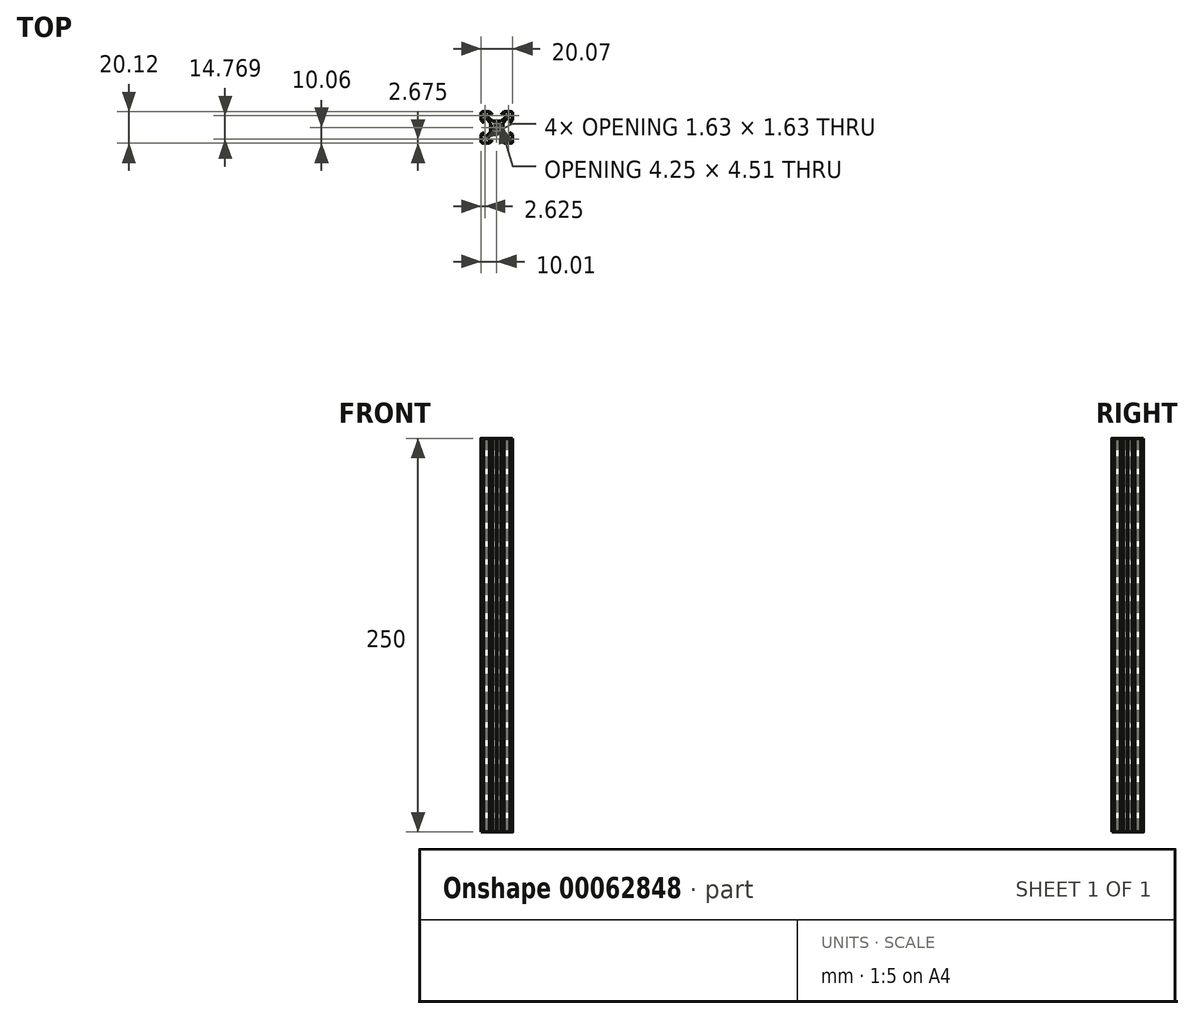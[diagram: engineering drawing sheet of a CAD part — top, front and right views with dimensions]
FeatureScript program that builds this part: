
annotation { "Feature Type Name" : "Feature", "Feature Type Description" : "" }
export const myFeature = defineFeature(function(context is Context, id is Id, definition is map)
    precondition{}
    {
        {
            var Q0;
            Q0=qCreatedBy(makeId("Top.planeOp"),FACE);
            var sketch = newSketch(context, id + "F0", { "sketchPlane" : qUnion([Q0])});
            skFitSpline(sketch, "E0", {"points": [v(-8.5, 10) * mm, v(-8.9, 10) * mm, v(-9.28, 9.84) * mm, v(-9.56, 9.56) * mm]});
            skFitSpline(sketch, "E1", {"points": [v(-9.56, 9.56) * mm, v(-9.84, 9.28) * mm, v(-10, 8.9) * mm, v(-10, 8.5) * mm]});
            skLineSegment(sketch, "E2", {"start": v(-10, 8.5) * mm, "end": v(-10, 4.64) * mm});
            skLineSegment(sketch, "E3", {"start": v(-10, 4.64) * mm, "end": v(-8.2, 2.84) * mm});
            skLineSegment(sketch, "E4", {"start": v(-8.2, 5.5) * mm, "end": v(-8.2, 2.84) * mm});
            skLineSegment(sketch, "E5", {"start": v(-8.2, 5.5) * mm, "end": v(-6.56, 5.5) * mm});
            skLineSegment(sketch, "E6", {"start": v(-6.56, 5.5) * mm, "end": v(-3.9, 2.84) * mm});
            skLineSegment(sketch, "E7", {"start": v(-3.9, 2.84) * mm, "end": v(-3.9, 0.2) * mm});
            skLineSegment(sketch, "E8", {"start": v(-3.9, 0.2) * mm, "end": v(-3.7, 0) * mm});
            skLineSegment(sketch, "E9", {"start": v(-3.9, -0.2) * mm, "end": v(-3.7, 0) * mm});
            skLineSegment(sketch, "E10", {"start": v(-3.9, -2.84) * mm, "end": v(-3.9, -0.2) * mm});
            skLineSegment(sketch, "E11", {"start": v(-6.56, -5.5) * mm, "end": v(-3.9, -2.84) * mm});
            skLineSegment(sketch, "E12", {"start": v(-8.2, -5.5) * mm, "end": v(-6.56, -5.5) * mm});
            skLineSegment(sketch, "E13", {"start": v(-8.2, -5.5) * mm, "end": v(-8.2, -2.84) * mm});
            skLineSegment(sketch, "E14", {"start": v(-10, -4.64) * mm, "end": v(-8.2, -2.84) * mm});
            skFitSpline(sketch, "E15", {"points": [v(-10, -8.5) * mm, v(-10, -8.9) * mm, v(-9.84, -9.28) * mm, v(-9.56, -9.56) * mm]});
            skFitSpline(sketch, "E16", {"points": [v(-9.56, -9.56) * mm, v(-9.28, -9.84) * mm, v(-8.9, -10) * mm, v(-8.5, -10) * mm]});
            skLineSegment(sketch, "E17", {"start": v(-10, -8.5) * mm, "end": v(-10, -4.64) * mm});
            skLineSegment(sketch, "E18", {"start": v(-8.5, -10) * mm, "end": v(-4.64, -10) * mm});
            skLineSegment(sketch, "E19", {"start": v(-4.64, -10) * mm, "end": v(-2.84, -8.2) * mm});
            skLineSegment(sketch, "E20", {"start": v(-2.84, -8.2) * mm, "end": v(-5.5, -8.2) * mm});
            skLineSegment(sketch, "E21", {"start": v(-5.5, -8.2) * mm, "end": v(-5.5, -6.56) * mm});
            skLineSegment(sketch, "E22", {"start": v(-5.5, -6.56) * mm, "end": v(-2.84, -3.9) * mm});
            skLineSegment(sketch, "E23", {"start": v(-0.2, -3.9) * mm, "end": v(-2.84, -3.9) * mm});
            skLineSegment(sketch, "E24", {"start": v(-0.2, -3.9) * mm, "end": v(0, -3.7) * mm});
            skLineSegment(sketch, "E25", {"start": v(0.2, -3.9) * mm, "end": v(0, -3.7) * mm});
            skLineSegment(sketch, "E26", {"start": v(0.2, -3.9) * mm, "end": v(2.84, -3.9) * mm});
            skLineSegment(sketch, "E27", {"start": v(5.5, -6.56) * mm, "end": v(2.84, -3.9) * mm});
            skLineSegment(sketch, "E28", {"start": v(5.5, -8.2) * mm, "end": v(5.5, -6.56) * mm});
            skLineSegment(sketch, "E29", {"start": v(2.84, -8.2) * mm, "end": v(5.5, -8.2) * mm});
            skLineSegment(sketch, "E30", {"start": v(4.64, -10) * mm, "end": v(2.84, -8.2) * mm});
            skFitSpline(sketch, "E31", {"points": [v(8.5, -10) * mm, v(9.33, -10) * mm, v(10, -9.33) * mm, v(10, -8.5) * mm]});
            skLineSegment(sketch, "E32", {"start": v(8.5, -10) * mm, "end": v(4.64, -10) * mm});
            skLineSegment(sketch, "E33", {"start": v(10, -8.5) * mm, "end": v(10, -4.64) * mm});
            skLineSegment(sketch, "E34", {"start": v(10, -4.64) * mm, "end": v(8.2, -2.84) * mm});
            skLineSegment(sketch, "E35", {"start": v(8.2, -5.5) * mm, "end": v(8.2, -2.84) * mm});
            skLineSegment(sketch, "E36", {"start": v(8.2, -5.5) * mm, "end": v(6.56, -5.5) * mm});
            skLineSegment(sketch, "E37", {"start": v(6.56, -5.5) * mm, "end": v(3.9, -2.84) * mm});
            skLineSegment(sketch, "E38", {"start": v(3.9, -2.84) * mm, "end": v(3.9, -0.2) * mm});
            skLineSegment(sketch, "E39", {"start": v(3.9, -0.2) * mm, "end": v(3.7, 0) * mm});
            skLineSegment(sketch, "E40", {"start": v(3.9, 0.2) * mm, "end": v(3.7, 0) * mm});
            skLineSegment(sketch, "E41", {"start": v(3.9, 2.84) * mm, "end": v(3.9, 0.2) * mm});
            skLineSegment(sketch, "E42", {"start": v(6.56, 5.5) * mm, "end": v(3.9, 2.84) * mm});
            skLineSegment(sketch, "E43", {"start": v(8.2, 5.5) * mm, "end": v(6.56, 5.5) * mm});
            skLineSegment(sketch, "E44", {"start": v(8.2, 5.5) * mm, "end": v(8.2, 2.84) * mm});
            skLineSegment(sketch, "E45", {"start": v(10, 4.64) * mm, "end": v(8.2, 2.84) * mm});
            skFitSpline(sketch, "E46", {"points": [v(10, 8.5) * mm, v(10, 9.33) * mm, v(9.33, 10) * mm, v(8.5, 10) * mm]});
            skLineSegment(sketch, "E47", {"start": v(10, 8.5) * mm, "end": v(10, 4.64) * mm});
            skLineSegment(sketch, "E48", {"start": v(8.5, 10) * mm, "end": v(4.64, 10) * mm});
            skLineSegment(sketch, "E49", {"start": v(4.64, 10) * mm, "end": v(2.84, 8.2) * mm});
            skLineSegment(sketch, "E50", {"start": v(2.84, 8.2) * mm, "end": v(5.5, 8.2) * mm});
            skLineSegment(sketch, "E51", {"start": v(5.5, 8.2) * mm, "end": v(5.5, 6.56) * mm});
            skLineSegment(sketch, "E52", {"start": v(5.5, 6.56) * mm, "end": v(2.84, 3.9) * mm});
            skLineSegment(sketch, "E53", {"start": v(0.2, 3.9) * mm, "end": v(2.84, 3.9) * mm});
            skLineSegment(sketch, "E54", {"start": v(0.2, 3.9) * mm, "end": v(0, 3.7) * mm});
            skLineSegment(sketch, "E55", {"start": v(-0.2, 3.9) * mm, "end": v(0, 3.7) * mm});
            skLineSegment(sketch, "E56", {"start": v(-0.2, 3.9) * mm, "end": v(-2.84, 3.9) * mm});
            skLineSegment(sketch, "E57", {"start": v(-5.5, 6.56) * mm, "end": v(-2.84, 3.9) * mm});
            skLineSegment(sketch, "E58", {"start": v(-5.5, 8.2) * mm, "end": v(-5.5, 6.56) * mm});
            skLineSegment(sketch, "E59", {"start": v(-2.84, 8.2) * mm, "end": v(-5.5, 8.2) * mm});
            skLineSegment(sketch, "E60", {"start": v(-4.64, 10) * mm, "end": v(-2.84, 8.2) * mm});
            skFitSpline(sketch, "E61", {"points": [v(2.1, 0) * mm, v(2.1, 0.75) * mm, v(1.7, 1.44) * mm, v(1.05, 1.82) * mm]});
            skFitSpline(sketch, "E62", {"points": [v(1.05, 1.82) * mm, v(0.4, 2.2) * mm, v(-0.4, 2.2) * mm, v(-1.05, 1.82) * mm]});
            skFitSpline(sketch, "E63", {"points": [v(-1.05, 1.82) * mm, v(-1.7, 1.44) * mm, v(-2.1, 0.75) * mm, v(-2.1, 0) * mm]});
            skFitSpline(sketch, "E64", {"points": [v(-2.1, 0) * mm, v(-2.1, -0.75) * mm, v(-1.7, -1.44) * mm, v(-1.05, -1.82) * mm]});
            skFitSpline(sketch, "E65", {"points": [v(-1.05, -1.82) * mm, v(-0.4, -2.2) * mm, v(0.4, -2.2) * mm, v(1.05, -1.82) * mm]});
            skFitSpline(sketch, "E66", {"points": [v(1.05, -1.82) * mm, v(1.7, -1.44) * mm, v(2.1, -0.75) * mm, v(2.1, 0) * mm]});
            skLineSegment(sketch, "E67", {"start": v(-8.5, 10) * mm, "end": v(-4.64, 10) * mm});
            skLineSegment(sketch, "E68", {"start": v(-6.57, 8.2) * mm, "end": v(-8.2, 8.2) * mm});
            skLineSegment(sketch, "E69", {"start": v(-6.57, 8.2) * mm, "end": v(-6.57, 7.63) * mm});
            skLineSegment(sketch, "E70", {"start": v(-7.63, 6.57) * mm, "end": v(-6.57, 7.63) * mm});
            skLineSegment(sketch, "E71", {"start": v(-8.2, 6.57) * mm, "end": v(-7.63, 6.57) * mm});
            skLineSegment(sketch, "E72", {"start": v(-8.2, 8.2) * mm, "end": v(-8.2, 6.57) * mm});
            skLineSegment(sketch, "E73", {"start": v(8.2, 8.2) * mm, "end": v(8.2, 6.57) * mm});
            skLineSegment(sketch, "E74", {"start": v(8.2, 6.57) * mm, "end": v(7.63, 6.57) * mm});
            skLineSegment(sketch, "E75", {"start": v(7.63, 6.57) * mm, "end": v(6.57, 7.63) * mm});
            skLineSegment(sketch, "E76", {"start": v(6.57, 8.2) * mm, "end": v(6.57, 7.63) * mm});
            skLineSegment(sketch, "E77", {"start": v(6.57, 8.2) * mm, "end": v(8.2, 8.2) * mm});
            skLineSegment(sketch, "E78", {"start": v(-8.2, -8.2) * mm, "end": v(-8.2, -6.57) * mm});
            skLineSegment(sketch, "E79", {"start": v(-8.2, -6.57) * mm, "end": v(-7.63, -6.57) * mm});
            skLineSegment(sketch, "E80", {"start": v(-7.63, -6.57) * mm, "end": v(-6.57, -7.63) * mm});
            skLineSegment(sketch, "E81", {"start": v(-6.57, -8.2) * mm, "end": v(-6.57, -7.63) * mm});
            skLineSegment(sketch, "E82", {"start": v(-6.57, -8.2) * mm, "end": v(-8.2, -8.2) * mm});
            skLineSegment(sketch, "E83", {"start": v(6.57, -8.2) * mm, "end": v(8.2, -8.2) * mm});
            skLineSegment(sketch, "E84", {"start": v(6.57, -8.2) * mm, "end": v(6.57, -7.63) * mm});
            skLineSegment(sketch, "E85", {"start": v(7.63, -6.57) * mm, "end": v(6.57, -7.63) * mm});
            skLineSegment(sketch, "E86", {"start": v(8.2, -6.57) * mm, "end": v(7.63, -6.57) * mm});
            skLineSegment(sketch, "E87", {"start": v(8.2, -8.2) * mm, "end": v(8.2, -6.57) * mm});
            skSolve(sketch);
        }
        {
            var Q0;
            Q0=makeQuery(id+"F0.imprint","IMPRINT",FACE,{"disambiguationData":[TD([[makeQuery(id+"F0.imprint","IMPRINT",EDGE,{"derivedFrom":sQuery(id+"F0.wireOp",EDGE,"E0")}),1.0]])]});
            extrude(context, id + "F1", {"entities" : qUnion([Q0]), "depth" : 250 * mm});
        }
    });
